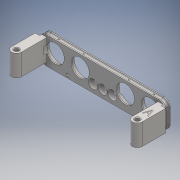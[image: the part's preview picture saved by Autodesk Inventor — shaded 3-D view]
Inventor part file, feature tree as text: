
AUTODESK INVENTOR PART (.ipt)
format: ipt  version: 2016 (Build 200138000, 138)  size: 327,168 bytes
history: native  units: mm
features: extrude x4, chamfer x4, sketch x4
ambient origin geometry x8: Origin, YZ Plane, XZ Plane, XY Plane, X Axis, Y Axis, Z Axis, Center Point
bodies: Solid2 (feature_tree), Solid1 (feature_tree)
feature tree (12):
  extrude  "Extrusion1"  Depth=6.79mm
  chamfer  "Chamfer1"  Distance=4.0mm
  extrude  "Extrusion2"  Depth=8.5mm
  chamfer  "Chamfer2"  Distance=8.5mm
  chamfer  "Chamfer3"  Distance=12.7mm
  chamfer  "Chamfer4"  Distance=3.2mm
  extrude  "Extrusion3"  Depth=4.0mm TaperAngle=0.0deg
  extrude  "Extrusion4"  Depth=2.0mm TaperAngle=30.0deg
  sketch  "Sketch1"  dims[d0=8.5mm d1=6.79mm d3=4.0mm d4=0.0mm]
  sketch  "Sketch2"  dims[d5=2.0mm d6=2.0mm d7=30.0deg d8=8.5mm]
  sketch  "Sketch3"  dims[d9=3.2mm]
  sketch  "Sketch4"  dims[d10=8.5mm d11=8.5mm d12=12.7mm d13=3.2mm d14=4.0mm d15=0.0mm d16=2.0mm d17=2.0mm d18=30.0deg d19=2.0mm d20=2.0mm d21=30.0deg d22=2.0mm d23=2.0mm d24=30.0deg d25=4.2mm d27=24.6mm d28=4.2mm d29=4.2mm d30=4.52mm d31=4.52mm d32=4.0mm d33=0.0mm d34=3.67mm d35=7.15mm d36=1.3mm d37=1.4mm d38=11.7mm d39=5.85mm d40=1.3mm d41=11.7mm d42=5.85mm d43=4.0mm d44=0.0mm]
